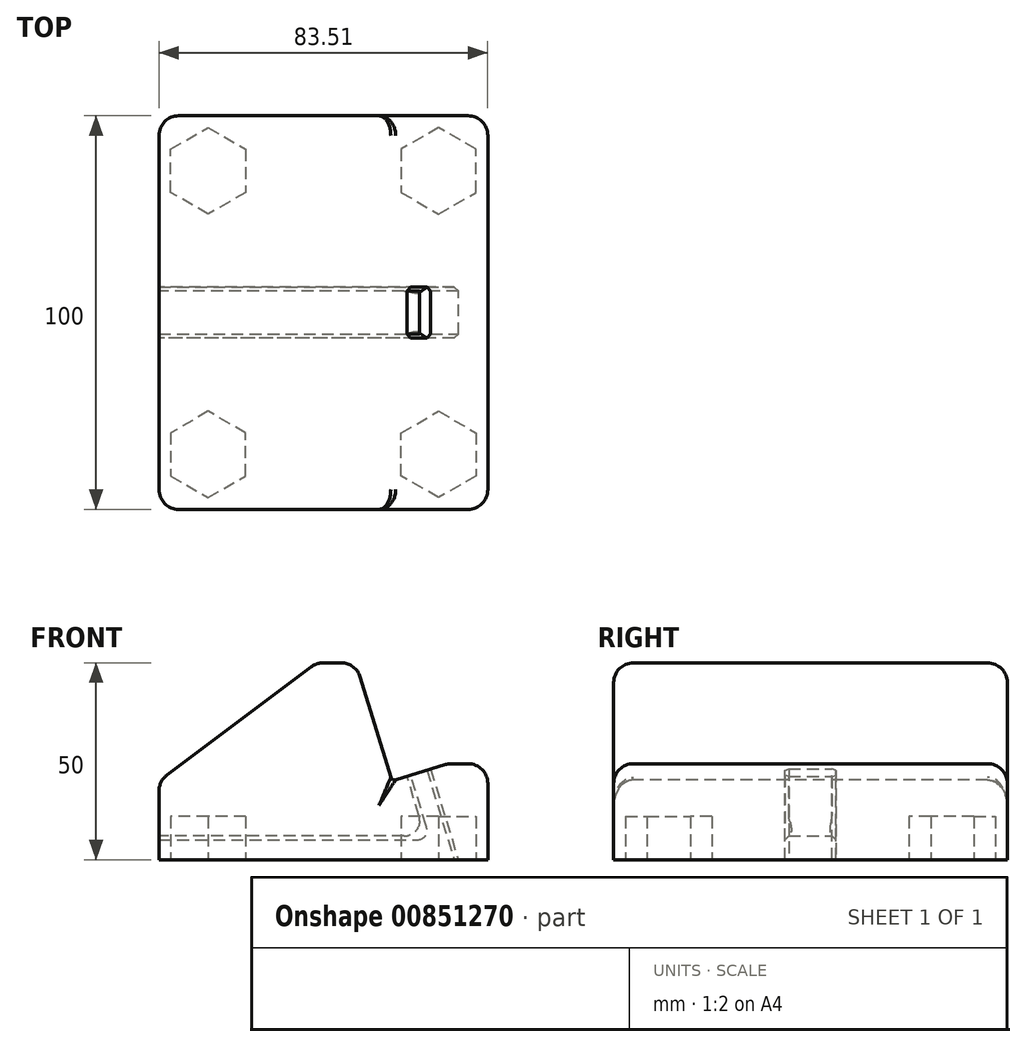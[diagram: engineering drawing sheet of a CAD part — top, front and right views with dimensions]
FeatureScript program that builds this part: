
annotation { "Feature Type Name" : "Feature", "Feature Type Description" : "" }
export const myFeature = defineFeature(function(context is Context, id is Id, definition is map)
    precondition{}
    {
        {
            var Q0;
            Q0=qCreatedBy(makeId("Front.planeOp"),FACE);
            var sketch = newSketch(context, id + "F0", { "sketchPlane" : qUnion([Q0])});
            skLineSegment(sketch, "E0.bottom", {"start": v(-19.17, -20) * mm, "end": v(24.34, -20) * mm});
            skLineSegment(sketch, "E0.top", {"start": v(-19.17, 30) * mm, "end": v(-9.17, 30) * mm});
            skLineSegment(sketch, "E0.left", {"start": v(-19.17, -20) * mm, "end": v(-19.17, 30) * mm, "construction": true});
            skLineSegment(sketch, "E1", {"start": v(-9.17, 30) * mm, "end": v(0, 0) * mm});
            skLineSegment(sketch, "E2", {"start": v(14.34, 4.39) * mm, "end": v(6.51, 30) * mm});
            skLineSegment(sketch, "E3", {"start": v(-19.17, -20) * mm, "end": v(-59.17, -20) * mm});
            skLineSegment(sketch, "E4", {"start": v(-59.17, -20) * mm, "end": v(-59.17, 0) * mm});
            skLineSegment(sketch, "E5", {"start": v(-59.17, 0) * mm, "end": v(-19.17, 30) * mm});
            skLineSegment(sketch, "E6", {"start": v(3.83, 1.17) * mm, "end": v(8.46, -14) * mm});
            skLineSegment(sketch, "E7", {"start": v(16.86, -20) * mm, "end": v(9.83, 3) * mm});
            skLineSegment(sketch, "E8", {"start": v(0, 0) * mm, "end": v(3.83, 1.17) * mm});
            skLineSegment(sketch, "E9", {"start": v(9.83, 3) * mm, "end": v(14.34, 4.39) * mm});
            skLineSegment(sketch, "E10", {"start": v(3.83, 1.17) * mm, "end": v(9.83, 3) * mm});
            skLineSegment(sketch, "E11", {"start": v(8.46, -14) * mm, "end": v(-59.17, -14) * mm});
            skLineSegment(sketch, "E12", {"start": v(24.34, 4.39) * mm, "end": v(21.9, 12.39) * mm});
            skArc(sketch, "E13", {"start": v(21.9, 12.39) * mm, "mid": v(16.9, 15.77) * mm, "end": v(11.9, 12.39) * mm});
            skLineSegment(sketch, "E14", {"start": v(24.34, 4.39) * mm, "end": v(24.34, -20) * mm});
            skLineSegment(sketch, "E15", {"start": v(14.34, 4.39) * mm, "end": v(24.34, 4.39) * mm});
            skSolve(sketch);
        }
        {
            var Q0;
            Q0=makeQuery(id+"F0.imprint","IMPRINT",FACE,{"disambiguationData":[TD([[makeQuery(id+"F0.imprint","IMPRINT",EDGE,{"derivedFrom":sQuery(id+"F0.wireOp",EDGE,"E0.bottom")}),1.0]])]});
            var Q1;
            Q1=makeQuery(id+"F0.imprint","IMPRINT",FACE,{"disambiguationData":[TD([[makeQuery(id+"F0.imprint","IMPRINT",EDGE,{"derivedFrom":sQuery(id+"F0.wireOp",EDGE,"E0.top")}),-1.0]])]});
            var Q2;
            {var subQ4=sQuery(id+"F0.wireOp",EDGE,"E3");Q2=makeQuery(id+"F0.imprint","IMPRINT",FACE,{"disambiguationData":[TD([[makeQuery(id+"F0.imprint","IMPRINT",EDGE,{"derivedFrom":subQ4}),-1.0]])]});}
            extrude(context, id + "F1", {"entities" : qUnion([Q0, Q1, Q2]), "endBound" : BoundingType.SYMMETRIC, "depth" : 100 * mm, "offsetDistance" : 25 * mm});
        }
        {
            var Q0;
            {var subQ4=sQuery(id+"F0.wireOp",EDGE,"E3");Q0=makeQuery(id+"F0.imprint","IMPRINT",FACE,{"disambiguationData":[TD([[makeQuery(id+"F0.imprint","IMPRINT",EDGE,{"derivedFrom":subQ4}),-1.0]])]});}
            extrude(context, id + "F2", {"entities" : qUnion([Q0]), "endBound" : BoundingType.SYMMETRIC, "depth" : 13 * mm, "offsetDistance" : 25 * mm});
        }
        {
            var Q0;
            Q0=makeQuery(id+"F2.opExtrude","CAP_EDGE",EDGE,{"disambiguationData":[OSD([sQuery(id+"F0.wireOp",EDGE,"E11")])],"isStart":false});
            var Q1;
            Q1=makeQuery(id+"F2.opExtrude","CAP_EDGE",EDGE,{"disambiguationData":[OSD([sQuery(id+"F0.wireOp",EDGE,"E11")])],"isStart":true});
            var Q2;
            Q2=makeQuery(id+"F2.opExtrude","CAP_EDGE",EDGE,{"disambiguationData":[OSD([sQuery(id+"F0.wireOp",EDGE,"E7")])],"isStart":true});
            var Q3;
            Q3=makeQuery(id+"F2.opExtrude","CAP_EDGE",EDGE,{"disambiguationData":[OSD([sQuery(id+"F0.wireOp",EDGE,"E7")])],"isStart":false});
            var Q4;
            Q4=makeQuery(id+"F2.opExtrude","CAP_EDGE",EDGE,{"disambiguationData":[OSD([sQuery(id+"F0.wireOp",EDGE,"E6")])],"isStart":false});
            var Q5;
            Q5=makeQuery(id+"F2.opExtrude","CAP_EDGE",EDGE,{"disambiguationData":[OSD([sQuery(id+"F0.wireOp",EDGE,"E6")])],"isStart":true});
            chamfer(context, id + "F3", {"entities" : qUnion([Q0, Q1, Q2, Q3, Q4, Q5]), "width" : 1 * mm, "tangentPropagation" : true});
        }
        {
            var Q0;
            Q0=makeQuery(id+"F2.opExtrude","SWEPT_FACE",FACE,{"disambiguationData":[OSD([sQuery(id+"F0.wireOp",EDGE,"E0.bottom"),sQuery(id+"F0.wireOp",EDGE,"E3")])]});
            var sketch = newSketch(context, id + "F4", { "sketchPlane" : qUnion([Q0])});
            skLineSegment(sketch, "E16.bottom", {"start": v(-44.17, 6.5) * mm, "end": v(-37.67, 6.5) * mm});
            skLineSegment(sketch, "E16.top", {"start": v(-44.17, 0) * mm, "end": v(-37.67, 0) * mm});
            skLineSegment(sketch, "E16.left", {"start": v(-44.17, 6.5) * mm, "end": v(-44.17, 0) * mm});
            skLineSegment(sketch, "E16.right", {"start": v(-37.67, 6.5) * mm, "end": v(-37.67, 0) * mm});
            skLineSegment(sketch, "E17.bottom", {"start": v(-21.17, -6.5) * mm, "end": v(-27.67, -6.5) * mm});
            skLineSegment(sketch, "E17.top", {"start": v(-21.17, 0) * mm, "end": v(-27.67, 0) * mm});
            skLineSegment(sketch, "E17.left", {"start": v(-21.17, -6.5) * mm, "end": v(-21.17, 0) * mm});
            skLineSegment(sketch, "E17.right", {"start": v(-27.67, -6.5) * mm, "end": v(-27.67, 0) * mm});
            skLineSegment(sketch, "E18.bottom", {"start": v(-4.67, 6.5) * mm, "end": v(-11.17, 6.5) * mm});
            skLineSegment(sketch, "E18.top", {"start": v(-4.67, 0) * mm, "end": v(-11.17, 0) * mm});
            skLineSegment(sketch, "E18.left", {"start": v(-4.67, 6.5) * mm, "end": v(-4.67, 0) * mm});
            skLineSegment(sketch, "E18.right", {"start": v(-11.17, 6.5) * mm, "end": v(-11.17, 0) * mm});
            skSolve(sketch);
        }
        {
            var Q0;
            Q0=makeQuery(id+"F4.imprint","IMPRINT",FACE,{"disambiguationData":[TD([[makeQuery(id+"F4.imprint","IMPRINT",EDGE,{"derivedFrom":sQuery(id+"F4.wireOp",EDGE,"E16.bottom")}),1.0]])]});
            var Q1;
            Q1=makeQuery(id+"F4.imprint","IMPRINT",FACE,{"disambiguationData":[TD([[makeQuery(id+"F4.imprint","IMPRINT",EDGE,{"derivedFrom":sQuery(id+"F4.wireOp",EDGE,"E17.bottom")}),-1.0]])]});
            var Q2;
            Q2=makeQuery(id+"F4.imprint","IMPRINT",FACE,{"disambiguationData":[TD([[makeQuery(id+"F4.imprint","IMPRINT",EDGE,{"derivedFrom":sQuery(id+"F4.wireOp",EDGE,"E18.bottom")}),1.0]])]});
            extrude(context, id + "F5", {"entities" : qUnion([Q0, Q1, Q2]), "operationType" : NewBodyOperationType.REMOVE, "oppositeDirection" : true, "depth" : 1.6 * mm, "offsetDistance" : 25 * mm});
        }
        {
            var Q0;
            Q0=makeQuery(id+"F5.boolean.opBoolean","COPY",EDGE,{"derivedFrom":makeQuery(id+"F5.opExtrude","SWEPT_EDGE",EDGE,{"disambiguationData":[OSD([sQuery(id+"F4.wireOp",EDGE,"E17.top"),sQuery(id+"F4.wireOp",EDGE,"E17.right")])]})});
            var Q1;
            Q1=makeQuery(id+"F5.boolean.opBoolean","COPY",EDGE,{"derivedFrom":makeQuery(id+"F5.opExtrude","SWEPT_EDGE",EDGE,{"disambiguationData":[OSD([sQuery(id+"F4.wireOp",EDGE,"E17.top"),sQuery(id+"F4.wireOp",EDGE,"E17.left")])]})});
            var Q2;
            Q2=makeQuery(id+"F5.boolean.opBoolean","COPY",EDGE,{"derivedFrom":makeQuery(id+"F5.opExtrude","SWEPT_EDGE",EDGE,{"disambiguationData":[OSD([sQuery(id+"F4.wireOp",EDGE,"E16.top"),sQuery(id+"F4.wireOp",EDGE,"E16.right")])]})});
            var Q3;
            Q3=makeQuery(id+"F5.boolean.opBoolean","COPY",EDGE,{"derivedFrom":makeQuery(id+"F5.opExtrude","SWEPT_EDGE",EDGE,{"disambiguationData":[OSD([sQuery(id+"F4.wireOp",EDGE,"E16.top"),sQuery(id+"F4.wireOp",EDGE,"E16.left")])]})});
            var Q4;
            Q4=makeQuery(id+"F5.boolean.opBoolean","COPY",EDGE,{"derivedFrom":makeQuery(id+"F5.opExtrude","SWEPT_EDGE",EDGE,{"disambiguationData":[OSD([sQuery(id+"F4.wireOp",EDGE,"E18.top"),sQuery(id+"F4.wireOp",EDGE,"E18.right")])]})});
            var Q5;
            Q5=makeQuery(id+"F5.boolean.opBoolean","COPY",EDGE,{"derivedFrom":makeQuery(id+"F5.opExtrude","SWEPT_EDGE",EDGE,{"disambiguationData":[OSD([sQuery(id+"F4.wireOp",EDGE,"E18.top"),sQuery(id+"F4.wireOp",EDGE,"E18.left")])]})});
            fillet(context, id + "F6", {"entities" : qUnion([Q0, Q1, Q2, Q3, Q4, Q5]), "radius" : 3 * mm, "tangentPropagation" : true, "allowEdgeOverflow" : false});
        }
        {
            var Q0;
            {var subQ0=sQuery(id+"F4.wireOp",EDGE,"E16.right");var subQ1=sQuery(id+"F4.wireOp",EDGE,"E16.top");Q0=makeQuery(id+"F6.opFillet","BLEND_EDGE",EDGE,{"blendedFrom":[makeQuery(id+"F5.boolean.opBoolean","COPY",EDGE,{"derivedFrom":makeQuery(id+"F5.opExtrude","SWEPT_EDGE",EDGE,{"disambiguationData":[OSD([subQ1,subQ0])]})}),makeQuery(id+"F5.boolean.opBoolean","COPY",FACE,{"derivedFrom":makeQuery(id+"F5.opExtrude","CAP_FACE",FACE,{"disambiguationData":[OSD([sQuery(id+"F4.wireOp",EDGE,"E16.bottom"),subQ1,sQuery(id+"F4.wireOp",EDGE,"E16.left"),subQ0])],"isStart":false})})],"blendedInto":[makeQuery(id+"F5.boolean.opBoolean","COPY",FACE,{"derivedFrom":makeQuery(id+"F5.opExtrude","CAP_FACE",FACE,{"disambiguationData":[OSD([sQuery(id+"F4.wireOp",EDGE,"E16.bottom"),subQ1,sQuery(id+"F4.wireOp",EDGE,"E16.left"),subQ0])],"isStart":false})})]});}
            var Q1;
            {var subQ0=sQuery(id+"F4.wireOp",EDGE,"E16.left");var subQ1=sQuery(id+"F4.wireOp",EDGE,"E16.top");Q1=makeQuery(id+"F6.opFillet","BLEND_EDGE",EDGE,{"blendedFrom":[makeQuery(id+"F5.boolean.opBoolean","COPY",EDGE,{"derivedFrom":makeQuery(id+"F5.opExtrude","SWEPT_EDGE",EDGE,{"disambiguationData":[OSD([subQ1,subQ0])]})}),makeQuery(id+"F5.boolean.opBoolean","COPY",FACE,{"derivedFrom":makeQuery(id+"F5.opExtrude","CAP_FACE",FACE,{"disambiguationData":[OSD([sQuery(id+"F4.wireOp",EDGE,"E16.bottom"),subQ1,subQ0,sQuery(id+"F4.wireOp",EDGE,"E16.right")])],"isStart":false})})],"blendedInto":[makeQuery(id+"F5.boolean.opBoolean","COPY",FACE,{"derivedFrom":makeQuery(id+"F5.opExtrude","CAP_FACE",FACE,{"disambiguationData":[OSD([sQuery(id+"F4.wireOp",EDGE,"E16.bottom"),subQ1,subQ0,sQuery(id+"F4.wireOp",EDGE,"E16.right")])],"isStart":false})})]});}
            var Q2;
            {var subQ0=sQuery(id+"F4.wireOp",EDGE,"E17.right");var subQ1=sQuery(id+"F4.wireOp",EDGE,"E17.top");Q2=makeQuery(id+"F6.opFillet","BLEND_EDGE",EDGE,{"blendedFrom":[makeQuery(id+"F5.boolean.opBoolean","COPY",EDGE,{"derivedFrom":makeQuery(id+"F5.opExtrude","SWEPT_EDGE",EDGE,{"disambiguationData":[OSD([subQ1,subQ0])]})}),makeQuery(id+"F5.boolean.opBoolean","COPY",FACE,{"derivedFrom":makeQuery(id+"F5.opExtrude","CAP_FACE",FACE,{"disambiguationData":[OSD([sQuery(id+"F4.wireOp",EDGE,"E17.bottom"),subQ1,sQuery(id+"F4.wireOp",EDGE,"E17.left"),subQ0])],"isStart":false})})],"blendedInto":[makeQuery(id+"F5.boolean.opBoolean","COPY",FACE,{"derivedFrom":makeQuery(id+"F5.opExtrude","CAP_FACE",FACE,{"disambiguationData":[OSD([sQuery(id+"F4.wireOp",EDGE,"E17.bottom"),subQ1,sQuery(id+"F4.wireOp",EDGE,"E17.left"),subQ0])],"isStart":false})})]});}
            var Q3;
            {var subQ0=sQuery(id+"F4.wireOp",EDGE,"E17.left");var subQ1=sQuery(id+"F4.wireOp",EDGE,"E17.top");Q3=makeQuery(id+"F6.opFillet","BLEND_EDGE",EDGE,{"blendedFrom":[makeQuery(id+"F5.boolean.opBoolean","COPY",EDGE,{"derivedFrom":makeQuery(id+"F5.opExtrude","SWEPT_EDGE",EDGE,{"disambiguationData":[OSD([subQ1,subQ0])]})}),makeQuery(id+"F5.boolean.opBoolean","COPY",FACE,{"derivedFrom":makeQuery(id+"F5.opExtrude","CAP_FACE",FACE,{"disambiguationData":[OSD([sQuery(id+"F4.wireOp",EDGE,"E17.bottom"),subQ1,subQ0,sQuery(id+"F4.wireOp",EDGE,"E17.right")])],"isStart":false})})],"blendedInto":[makeQuery(id+"F5.boolean.opBoolean","COPY",FACE,{"derivedFrom":makeQuery(id+"F5.opExtrude","CAP_FACE",FACE,{"disambiguationData":[OSD([sQuery(id+"F4.wireOp",EDGE,"E17.bottom"),subQ1,subQ0,sQuery(id+"F4.wireOp",EDGE,"E17.right")])],"isStart":false})})]});}
            var Q4;
            Q4=makeQuery(id+"F5.boolean.opBoolean","COPY",EDGE,{"derivedFrom":makeQuery(id+"F5.opExtrude","CAP_EDGE",EDGE,{"disambiguationData":[OSD([sQuery(id+"F4.wireOp",EDGE,"E17.top")])],"isStart":false})});
            var Q5;
            Q5=makeQuery(id+"F5.boolean.opBoolean","COPY",EDGE,{"derivedFrom":makeQuery(id+"F5.opExtrude","CAP_EDGE",EDGE,{"disambiguationData":[OSD([sQuery(id+"F4.wireOp",EDGE,"E16.top")])],"isStart":false})});
            var Q6;
            {var subQ0=sQuery(id+"F4.wireOp",EDGE,"E18.left");var subQ1=sQuery(id+"F4.wireOp",EDGE,"E18.top");Q6=makeQuery(id+"F6.opFillet","BLEND_EDGE",EDGE,{"blendedFrom":[makeQuery(id+"F5.boolean.opBoolean","COPY",EDGE,{"derivedFrom":makeQuery(id+"F5.opExtrude","SWEPT_EDGE",EDGE,{"disambiguationData":[OSD([subQ1,subQ0])]})}),makeQuery(id+"F5.boolean.opBoolean","COPY",FACE,{"derivedFrom":makeQuery(id+"F5.opExtrude","CAP_FACE",FACE,{"disambiguationData":[OSD([sQuery(id+"F4.wireOp",EDGE,"E18.bottom"),subQ1,subQ0,sQuery(id+"F4.wireOp",EDGE,"E18.right")])],"isStart":false})})],"blendedInto":[makeQuery(id+"F5.boolean.opBoolean","COPY",FACE,{"derivedFrom":makeQuery(id+"F5.opExtrude","CAP_FACE",FACE,{"disambiguationData":[OSD([sQuery(id+"F4.wireOp",EDGE,"E18.bottom"),subQ1,subQ0,sQuery(id+"F4.wireOp",EDGE,"E18.right")])],"isStart":false})})]});}
            chamfer(context, id + "F7", {"entities" : qUnion([Q0, Q1, Q2, Q3, Q4, Q5, Q6]), "chamferType" : ChamferType.TWO_OFFSETS, "width1" : 0.8 * mm, "oppositeDirection" : false, "width2" : 1.6 * mm, "tangentPropagation" : true});
        }
        {
            var Q0;
            Q0=makeQuery(id+"F2.opExtrude","SWEPT_BODY",BODY,{"disambiguationData":[OSD([sQuery(id+"F0.wireOp",EDGE,"E0.bottom"),sQuery(id+"F0.wireOp",EDGE,"E3"),sQuery(id+"F0.wireOp",EDGE,"E4"),sQuery(id+"F0.wireOp",EDGE,"E6"),sQuery(id+"F0.wireOp",EDGE,"E7"),sQuery(id+"F0.wireOp",EDGE,"E10"),sQuery(id+"F0.wireOp",EDGE,"E11"),sQuery(id+"F0.wireOp",EDGE,"pMoNHxmZ-PZBw-MJiK-MIso-0IMV9dccQYyO")])]});
            var Q1;
            Q1=makeQuery(id+"F1.opExtrude","SWEPT_BODY",BODY,{"disambiguationData":[OSD([sQuery(id+"F0.wireOp",EDGE,"E0.bottom"),sQuery(id+"F0.wireOp",EDGE,"E0.top"),sQuery(id+"F0.wireOp",EDGE,"E1"),sQuery(id+"F0.wireOp",EDGE,"E2"),sQuery(id+"F0.wireOp",EDGE,"E3"),sQuery(id+"F0.wireOp",EDGE,"E4"),sQuery(id+"F0.wireOp",EDGE,"E5"),sQuery(id+"F0.wireOp",EDGE,"E8"),sQuery(id+"F0.wireOp",EDGE,"E9"),sQuery(id+"F0.wireOp",EDGE,"E10"),sQuery(id+"F0.wireOp",EDGE,"E12"),sQuery(id+"F0.wireOp",EDGE,"E13"),sQuery(id+"F0.wireOp",EDGE,"E14")])]});
            booleanBodies(context, id + "F8", {"operationType" : BooleanOperationType.SUBTRACTION, "tools" : qUnion([Q0]), "targets" : qUnion([Q1])});
        }
        {
            var Q0;
            Q0=makeQuery(id+"F8.opBoolean","COPY",EDGE,{"derivedFrom":makeQuery(id+"F2.opExtrude","SWEPT_EDGE",EDGE,{"disambiguationData":[OSD([sQuery(id+"F0.wireOp",EDGE,"E6"),sQuery(id+"F0.wireOp",EDGE,"E11")])]})});
            var Q1;
            Q1=makeQuery(id+"F8.opBoolean","COPY",EDGE,{"derivedFrom":makeQuery(id+"F3.opChamfer","BLEND_EDGE",EDGE,{"blendedFrom":[makeQuery(id+"F2.opExtrude","CAP_EDGE",EDGE,{"disambiguationData":[OSD([sQuery(id+"F0.wireOp",EDGE,"E6")])],"isStart":true}),makeQuery(id+"F2.opExtrude","CAP_EDGE",EDGE,{"disambiguationData":[OSD([sQuery(id+"F0.wireOp",EDGE,"E11")])],"isStart":true})],"blendedInto":[]})});
            var Q2;
            Q2=makeQuery(id+"F8.opBoolean","COPY",EDGE,{"derivedFrom":makeQuery(id+"F3.opChamfer","BLEND_EDGE",EDGE,{"blendedFrom":[makeQuery(id+"F2.opExtrude","CAP_EDGE",EDGE,{"disambiguationData":[OSD([sQuery(id+"F0.wireOp",EDGE,"E6")])],"isStart":false}),makeQuery(id+"F2.opExtrude","CAP_EDGE",EDGE,{"disambiguationData":[OSD([sQuery(id+"F0.wireOp",EDGE,"E11")])],"isStart":false})],"blendedInto":[]})});
            fillet(context, id + "F9", {"entities" : qUnion([Q0, Q1, Q2]), "radius" : 4 * mm, "tangentPropagation" : true, "allowEdgeOverflow" : false});
        }
        {
            var Q0;
            Q0=makeQuery(id+"F1.opExtrude","SWEPT_EDGE",EDGE,{"disambiguationData":[OSD([sQuery(id+"F0.wireOp",EDGE,"E12"),sQuery(id+"F0.wireOp",EDGE,"E14"),sQuery(id+"F0.wireOp",EDGE,"E15")])]});
            var Q1;
            Q1=makeQuery(id+"F1.opExtrude","SWEPT_EDGE",EDGE,{"disambiguationData":[OSD([sQuery(id+"F0.wireOp",EDGE,"E0.top"),sQuery(id+"F0.wireOp",EDGE,"E1")])]});
            var Q2;
            Q2=makeQuery(id+"F1.opExtrude","CAP_EDGE",EDGE,{"disambiguationData":[OSD([sQuery(id+"F0.wireOp",EDGE,"E14")])],"isStart":true});
            var Q3;
            Q3=makeQuery(id+"F1.opExtrude","CAP_EDGE",EDGE,{"disambiguationData":[OSD([sQuery(id+"F0.wireOp",EDGE,"E1")])],"isStart":true});
            var Q4;
            Q4=makeQuery(id+"F1.opExtrude","CAP_EDGE",EDGE,{"disambiguationData":[OSD([sQuery(id+"F0.wireOp",EDGE,"E0.top")])],"isStart":true});
            var Q5;
            Q5=makeQuery(id+"F1.opExtrude","CAP_EDGE",EDGE,{"disambiguationData":[OSD([sQuery(id+"F0.wireOp",EDGE,"E5")])],"isStart":true});
            var Q6;
            Q6=makeQuery(id+"F1.opExtrude","CAP_EDGE",EDGE,{"disambiguationData":[OSD([sQuery(id+"F0.wireOp",EDGE,"E4")])],"isStart":true});
            var Q7;
            Q7=makeQuery(id+"F1.opExtrude","SWEPT_EDGE",EDGE,{"disambiguationData":[OSD([sQuery(id+"F0.wireOp",EDGE,"E4"),sQuery(id+"F0.wireOp",EDGE,"E5")])]});
            var Q8;
            Q8=makeQuery(id+"F1.opExtrude","SWEPT_EDGE",EDGE,{"disambiguationData":[OSD([sQuery(id+"F0.wireOp",EDGE,"E0.top"),sQuery(id+"F0.wireOp",EDGE,"E5")])]});
            var Q9;
            Q9=makeQuery(id+"F1.opExtrude","CAP_EDGE",EDGE,{"disambiguationData":[OSD([sQuery(id+"F0.wireOp",EDGE,"E5")])],"isStart":false});
            var Q10;
            Q10=makeQuery(id+"F1.opExtrude","CAP_EDGE",EDGE,{"disambiguationData":[OSD([sQuery(id+"F0.wireOp",EDGE,"E4")])],"isStart":false});
            var Q11;
            Q11=makeQuery(id+"F1.opExtrude","CAP_EDGE",EDGE,{"disambiguationData":[OSD([sQuery(id+"F0.wireOp",EDGE,"E0.top")])],"isStart":false});
            var Q12;
            Q12=makeQuery(id+"F1.opExtrude","CAP_EDGE",EDGE,{"disambiguationData":[OSD([sQuery(id+"F0.wireOp",EDGE,"E1")])],"isStart":false});
            var Q13;
            Q13=makeQuery(id+"F1.opExtrude","CAP_EDGE",EDGE,{"disambiguationData":[OSD([sQuery(id+"F0.wireOp",EDGE,"E14")])],"isStart":false});
            var Q14;
            Q14=makeQuery(id+"F1.opExtrude","CAP_EDGE",EDGE,{"disambiguationData":[OSD([sQuery(id+"F0.wireOp",EDGE,"E12")])],"isStart":true});
            var Q15;
            Q15=makeQuery(id+"F1.opExtrude","CAP_EDGE",EDGE,{"disambiguationData":[OSD([sQuery(id+"F0.wireOp",EDGE,"E12")])],"isStart":false});
            var Q16;
            Q16=makeQuery(id+"F1.opExtrude","CAP_EDGE",EDGE,{"disambiguationData":[OSD([sQuery(id+"F0.wireOp",EDGE,"E8"),sQuery(id+"F0.wireOp",EDGE,"E9"),sQuery(id+"F0.wireOp",EDGE,"E10")])],"isStart":false});
            var Q17;
            Q17=makeQuery(id+"F1.opExtrude","CAP_EDGE",EDGE,{"disambiguationData":[OSD([sQuery(id+"F0.wireOp",EDGE,"E8"),sQuery(id+"F0.wireOp",EDGE,"E9"),sQuery(id+"F0.wireOp",EDGE,"E10")])],"isStart":true});
            var Q18;
            Q18=makeQuery(id+"F1.opExtrude","CAP_EDGE",EDGE,{"disambiguationData":[OSD([sQuery(id+"F0.wireOp",EDGE,"E15")])],"isStart":false});
            var Q19;
            Q19=makeQuery(id+"F1.opExtrude","CAP_EDGE",EDGE,{"disambiguationData":[OSD([sQuery(id+"F0.wireOp",EDGE,"E15")])],"isStart":true});
            var Q20;
            Q20=makeQuery(id+"F1.opExtrude","SWEPT_EDGE",EDGE,{"disambiguationData":[OSD([sQuery(id+"F0.wireOp",EDGE,"E2"),sQuery(id+"F0.wireOp",EDGE,"E9"),sQuery(id+"F0.wireOp",EDGE,"E15")])]});
            fillet(context, id + "F10", {"entities" : qUnion([Q0, Q1, Q2, Q3, Q4, Q5, Q6, Q7, Q8, Q9, Q10, Q11, Q12, Q13, Q14, Q15, Q16, Q17, Q18, Q19, Q20]), "radius" : 5 * mm, "tangentPropagation" : true, "allowEdgeOverflow" : false});
        }
        {
            var Q0;
            Q0=makeQuery(id+"F1.opExtrude","SWEPT_FACE",FACE,{"disambiguationData":[OSD([sQuery(id+"F0.wireOp",EDGE,"E0.bottom"),sQuery(id+"F0.wireOp",EDGE,"E3")])]});
            var sketch = newSketch(context, id + "F11", { "sketchPlane" : qUnion([Q0])});
            skCircle(sketch, "E19.cCircle", {"center": v(-46.67, 36.03) * mm, "radius": 9.5 * mm, "construction": true});
            skLineSegment(sketch, "E19.0", {"start": v(-37.17, 41.52) * mm, "end": v(-37.17, 30.55) * mm});
            skLineSegment(sketch, "E19.1", {"start": v(-37.17, 30.55) * mm, "end": v(-46.67, 25.06) * mm});
            skLineSegment(sketch, "E19.2", {"start": v(-46.67, 25.06) * mm, "end": v(-56.17, 30.55) * mm});
            skLineSegment(sketch, "E19.3", {"start": v(-56.17, 30.55) * mm, "end": v(-56.17, 41.52) * mm});
            skLineSegment(sketch, "E19.4", {"start": v(-56.17, 41.52) * mm, "end": v(-46.67, 47) * mm});
            skLineSegment(sketch, "E19.5", {"start": v(-46.67, 47) * mm, "end": v(-37.17, 41.52) * mm});
            skPoint(sketch, "E19.0.midPoint", {"position": v(-37.17, 36.03) * mm});
            skLineSegment(sketch, "E20", {"start": v(-59.17, 0) * mm, "end": v(24.34, 0) * mm, "construction": true});
            skPoint(sketch, "E20.startSnap0", {"position": v(-57.7, 48.54) * mm});
            skPoint(sketch, "E21", {"position": v(-17.41, 0) * mm});
            skLineSegment(sketch, "E22.MirrorCS", {"start": v(-37.17, -30.55) * mm, "end": v(-46.67, -25.06) * mm});
            skLineSegment(sketch, "E23.MirrorCS", {"start": v(-46.67, -25.06) * mm, "end": v(-56.17, -30.55) * mm});
            skLineSegment(sketch, "E24.MirrorCS", {"start": v(-56.17, -30.55) * mm, "end": v(-56.17, -41.52) * mm});
            skLineSegment(sketch, "E25.MirrorCS", {"start": v(-56.17, -41.52) * mm, "end": v(-46.67, -47) * mm});
            skLineSegment(sketch, "E26.MirrorCS", {"start": v(-46.67, -47) * mm, "end": v(-37.17, -41.52) * mm});
            skLineSegment(sketch, "E27.MirrorCS", {"start": v(-37.17, -41.52) * mm, "end": v(-37.17, -30.55) * mm});
            skLineSegment(sketch, "E28", {"start": v(-17.41, 0) * mm, "end": v(-17.41, 50) * mm, "construction": true});
            skLineSegment(sketch, "E29.MirrorCS", {"start": v(2.34, 41.52) * mm, "end": v(2.34, 30.55) * mm});
            skLineSegment(sketch, "E30.MirrorCS", {"start": v(2.34, 30.55) * mm, "end": v(11.84, 25.06) * mm});
            skLineSegment(sketch, "E31.MirrorCS", {"start": v(11.84, 25.06) * mm, "end": v(21.34, 30.55) * mm});
            skLineSegment(sketch, "E32.MirrorCS", {"start": v(21.34, 30.55) * mm, "end": v(21.34, 41.52) * mm});
            skLineSegment(sketch, "E33.MirrorCS", {"start": v(21.34, 41.52) * mm, "end": v(11.84, 47) * mm});
            skLineSegment(sketch, "E34.MirrorCS", {"start": v(11.84, 47) * mm, "end": v(2.34, 41.52) * mm});
            skLineSegment(sketch, "E35.MirrorCS", {"start": v(2.34, -41.52) * mm, "end": v(2.34, -30.55) * mm});
            skLineSegment(sketch, "E36.MirrorCS", {"start": v(2.34, -30.55) * mm, "end": v(11.84, -25.06) * mm});
            skLineSegment(sketch, "E37.MirrorCS", {"start": v(11.84, -47) * mm, "end": v(2.34, -41.52) * mm});
            skLineSegment(sketch, "E38.MirrorCS", {"start": v(21.34, -41.52) * mm, "end": v(11.84, -47) * mm});
            skLineSegment(sketch, "E39.MirrorCS", {"start": v(21.34, -30.55) * mm, "end": v(21.34, -41.52) * mm});
            skLineSegment(sketch, "E40.MirrorCS", {"start": v(11.84, -25.06) * mm, "end": v(21.34, -30.55) * mm});
            skSolve(sketch);
        }
        {
            var Q0;
            Q0=makeQuery(id+"F11.imprint","IMPRINT",FACE,{"disambiguationData":[TD([[makeQuery(id+"F11.imprint","IMPRINT",EDGE,{"derivedFrom":sQuery(id+"F11.wireOp",EDGE,"E22.MirrorCS")}),1.0]])]});
            var Q1;
            Q1=makeQuery(id+"F11.imprint","IMPRINT",FACE,{"disambiguationData":[TD([[makeQuery(id+"F11.imprint","IMPRINT",EDGE,{"derivedFrom":sQuery(id+"F11.wireOp",EDGE,"E19.0")}),-1.0]])]});
            var Q2;
            Q2=makeQuery(id+"F11.imprint","IMPRINT",FACE,{"disambiguationData":[TD([[makeQuery(id+"F11.imprint","IMPRINT",EDGE,{"derivedFrom":sQuery(id+"F11.wireOp",EDGE,"E29.MirrorCS")}),1.0]])]});
            var Q3;
            Q3=makeQuery(id+"F11.imprint","IMPRINT",FACE,{"disambiguationData":[TD([[makeQuery(id+"F11.imprint","IMPRINT",EDGE,{"derivedFrom":sQuery(id+"F11.wireOp",EDGE,"E35.MirrorCS")}),-1.0]])]});
            extrude(context, id + "F12", {"entities" : qUnion([Q0, Q1, Q2, Q3]), "operationType" : NewBodyOperationType.REMOVE, "oppositeDirection" : true, "depth" : 11 * mm, "offsetDistance" : 25 * mm});
        }
        {
            var Q0;
            Q0=makeQuery(id+"F1.opExtrude","SWEPT_EDGE",EDGE,{"disambiguationData":[OSD([sQuery(id+"F0.wireOp",EDGE,"E1"),sQuery(id+"F0.wireOp",EDGE,"E8")])]});
            fillet(context, id + "F13", {"entities" : qUnion([Q0]), "radius" : 1 * mm, "tangentPropagation" : true, "allowEdgeOverflow" : false});
        }
    });
